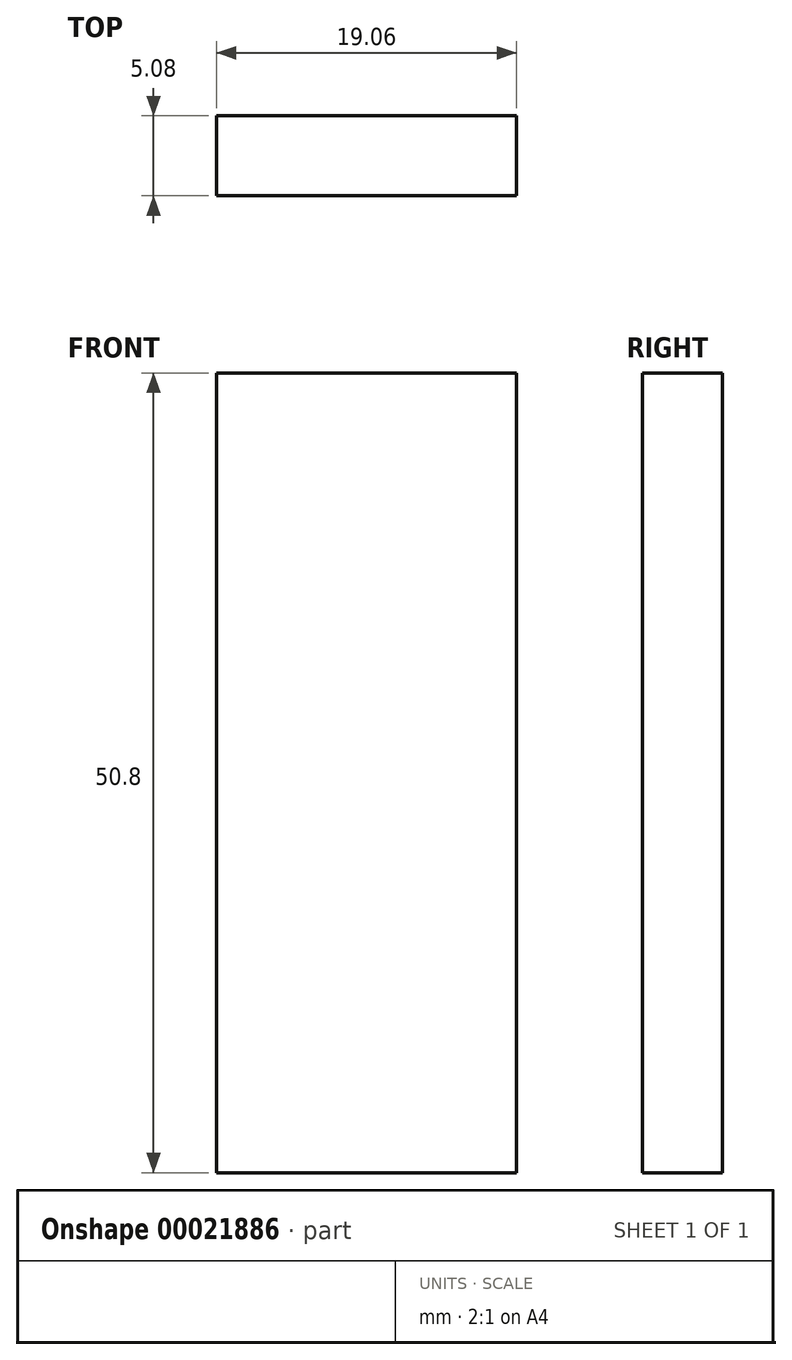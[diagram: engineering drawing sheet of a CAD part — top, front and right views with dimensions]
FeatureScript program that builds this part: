
annotation { "Feature Type Name" : "Feature", "Feature Type Description" : "" }
export const myFeature = defineFeature(function(context is Context, id is Id, definition is map)
    precondition{}
    {
        {
            var Q0;
            Q0=qCreatedBy(makeId("Front.planeOp"),FACE);
            var sketch = newSketch(context, id + "F0", { "sketchPlane" : qUnion([Q0])});
            skLineSegment(sketch, "E0.rect.bottom", {"start": v(9.53, 25.4) * mm, "end": v(-9.52, 25.4) * mm});
            skLineSegment(sketch, "E0.rect.top", {"start": v(9.52, -25.4) * mm, "end": v(-9.53, -25.4) * mm});
            skLineSegment(sketch, "E0.rect.left", {"start": v(9.53, 25.4) * mm, "end": v(9.52, -25.4) * mm});
            skLineSegment(sketch, "E0.rect.right", {"start": v(-9.52, 25.4) * mm, "end": v(-9.53, -25.4) * mm});
            skPoint(sketch, "E0.rect.middle", {"position": v(0, 0) * mm});
            skSolve(sketch);
        }
        {
            var Q0;
            Q0 = qSketchRegion(id + "F0", true);
            extrude(context, id + "F1", {"entities" : qUnion([Q0]), "depth" : 5.08 * mm});
        }
    });
